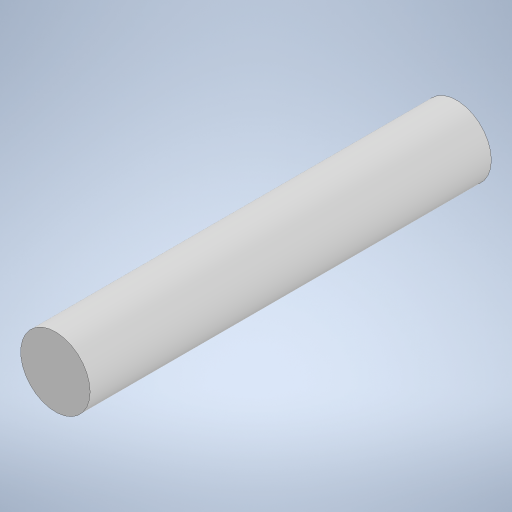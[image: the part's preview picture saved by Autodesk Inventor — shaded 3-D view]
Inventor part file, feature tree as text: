
AUTODESK INVENTOR PART (.ipt)
format: ipt  version: 2023 (Build 270158000, 158)  size: 216,576 bytes
history: native  units: in
note: dims shown in document units (in); Inventor stores cm internally (conversion verified against a paired STEP export)
features: extrude x1, sketch x1
ambient origin geometry x8: Origin, YZ Plane, XZ Plane, XY Plane, X Axis, Y Axis, Z Axis, Center Point
bodies: Solid1 (feature_tree)
feature tree (2):
  extrude  "Extrusion1"  Depth=0.4547in TaperAngle=0.0deg
  sketch  "Sketch1"  dims[d0=0.0787in d1=0.4547in d2=0.0in]
